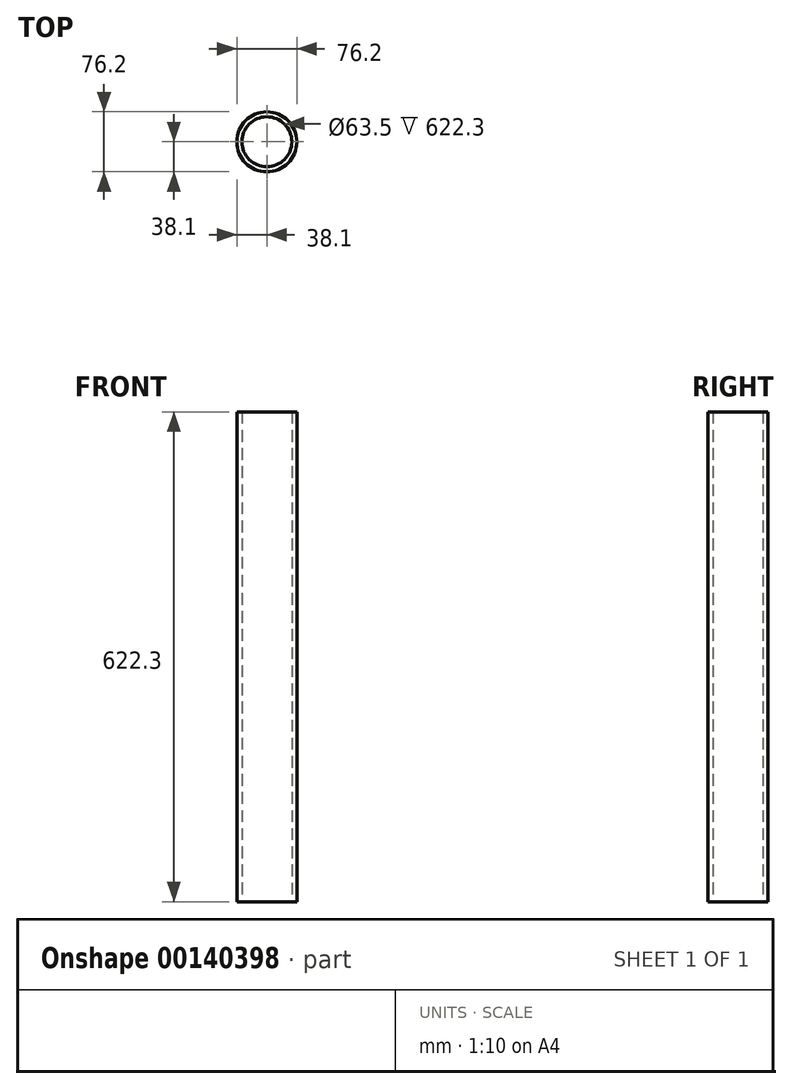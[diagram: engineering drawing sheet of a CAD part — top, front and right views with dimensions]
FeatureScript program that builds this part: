
annotation { "Feature Type Name" : "Feature", "Feature Type Description" : "" }
export const myFeature = defineFeature(function(context is Context, id is Id, definition is map)
    precondition{}
    {
        {
            var Q0;
            Q0=qCreatedBy(makeId("Top.planeOp"),FACE);
            var sketch = newSketch(context, id + "F0", { "sketchPlane" : qUnion([Q0])});
            skCircle(sketch, "E0", {"center": v(0, 0) * mm, "radius": 38.1 * mm});
            skCircle(sketch, "E1.0", {"center": v(0, 0) * mm, "radius": 31.75 * mm});
            skSolve(sketch);
        }
        {
            var Q0;
            Q0=makeQuery(id+"F0.imprint","IMPRINT",FACE,{"disambiguationData":[TD([[makeQuery(id+"F0.imprint","IMPRINT",EDGE,{"derivedFrom":sQuery(id+"F0.wireOp",EDGE,"E0")}),1.0]])]});
            extrude(context, id + "F1", {"entities" : qUnion([Q0]), "depth" : 622.3 * mm});
        }
    });
